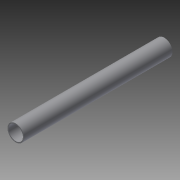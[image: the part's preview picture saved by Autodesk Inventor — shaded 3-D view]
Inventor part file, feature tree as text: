
AUTODESK INVENTOR PART (.ipt)
format: ipt  version: 2014 (Build 180170000, 170)  size: 71,168 bytes
history: native  units: in
note: dims shown in document units (in); Inventor stores cm internally (conversion verified against a paired STEP export)
features: extrude x1, sketch x1
ambient origin geometry x8: Origin, YZ Plane, XZ Plane, XY Plane, X Axis, Y Axis, Z Axis, Center Point
bodies: Solid1 (feature_tree)
feature tree (2):
  extrude  "Extrusion1"  Depth=9.0in
  sketch  "Sketch1"  dims[d0=1.0in d1=0.875in d2=9.0in d3=0.0in]
